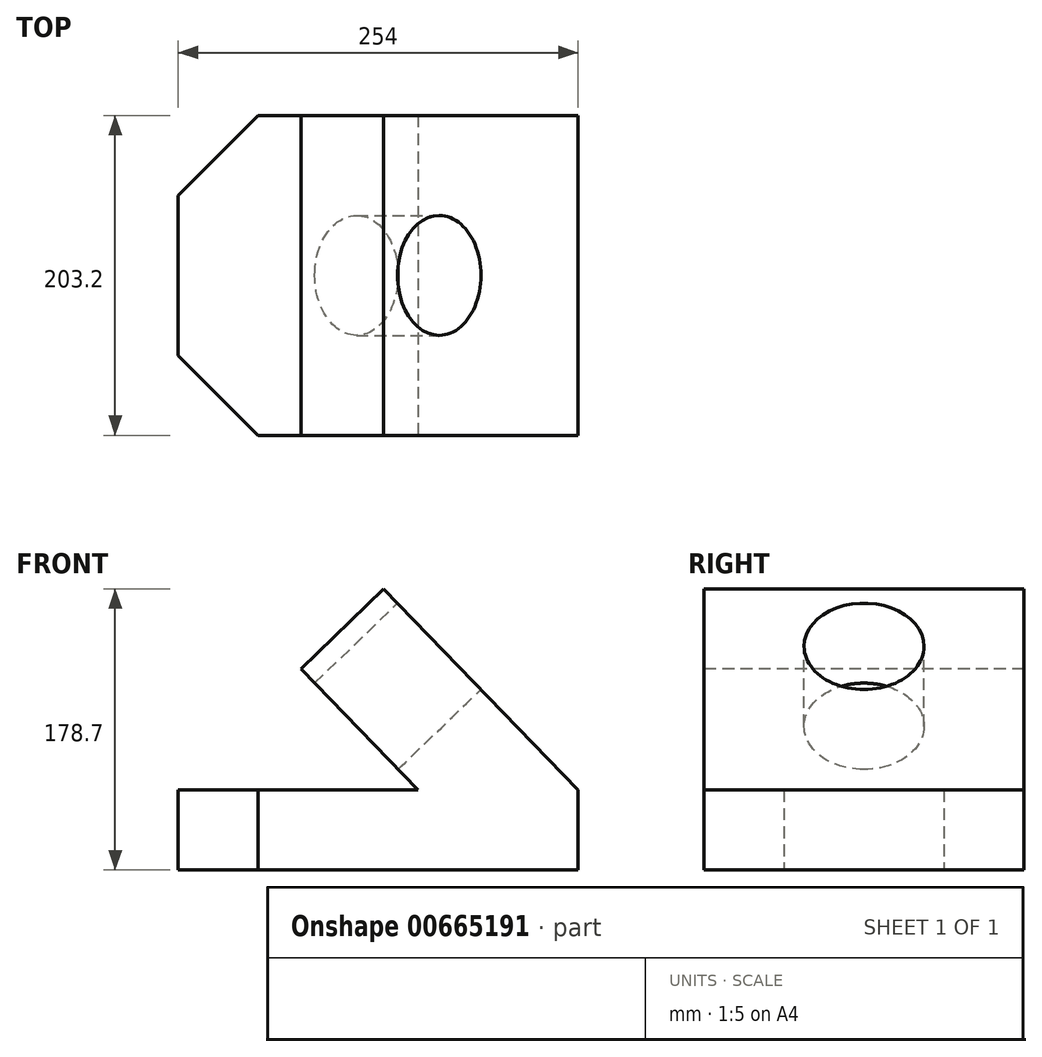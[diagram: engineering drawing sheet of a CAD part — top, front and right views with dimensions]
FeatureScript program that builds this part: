
annotation { "Feature Type Name" : "Feature", "Feature Type Description" : "" }
export const myFeature = defineFeature(function(context is Context, id is Id, definition is map)
    precondition{}
    {
        {
            var Q0;
            Q0=qCreatedBy(makeId("Top.planeOp"),FACE);
            var sketch = newSketch(context, id + "F0", { "sketchPlane" : qUnion([Q0])});
            skLineSegment(sketch, "E0", {"start": v(0, 0) * mm, "end": v(203.2, 0) * mm});
            skLineSegment(sketch, "E1", {"start": v(203.2, 0) * mm, "end": v(203.2, 203.2) * mm});
            skLineSegment(sketch, "E2", {"start": v(203.2, 203.2) * mm, "end": v(0, 203.2) * mm});
            skLineSegment(sketch, "E3", {"start": v(0, 203.2) * mm, "end": v(-50.8, 152.4) * mm});
            skLineSegment(sketch, "E4", {"start": v(-50.8, 152.4) * mm, "end": v(-50.8, 50.8) * mm});
            skLineSegment(sketch, "E5", {"start": v(-50.8, 50.8) * mm, "end": v(0, 0) * mm});
            skSolve(sketch);
        }
        {
            var Q0;
            Q0=makeQuery(id+"F0.imprint","IMPRINT",FACE,{"disambiguationData":[TD([[makeQuery(id+"F0.imprint","IMPRINT",EDGE,{"derivedFrom":sQuery(id+"F0.wireOp",EDGE,"E0")}),1.0]])]});
            extrude(context, id + "F1", {"entities" : qUnion([Q0]), "endBound" : BoundingType.SYMMETRIC, "depth" : 50.8 * mm, "offsetDistance" : 25.4 * mm});
        }
        {
            var Q0;
            Q0=makeQuery(id+"F1.opExtrude","CAP_EDGE",EDGE,{"disambiguationData":[OSD([sQuery(id+"F0.wireOp",EDGE,"E1")])],"isStart":false});
            cPlane(context, id + "F2", {"entities" : qUnion([Q0]), "cplaneType" : CPlaneType.LINE_ANGLE, "offset" : 25.4 * mm, "angle" : 46 * degree, "width" : 152.4 * mm, "height" : 152.4 * mm});
        }
        {
            var Q0;
            Q0=qCreatedBy(id+"F2.planeOp",FACE);
            var sketch = newSketch(context, id + "F3", { "sketchPlane" : qUnion([Q0])});
            skLineSegment(sketch, "E6", {"start": v(203.2, 54.92) * mm, "end": v(0, 54.92) * mm});
            skLineSegment(sketch, "E7", {"start": v(203.2, -122.88) * mm, "end": v(0, -122.88) * mm});
            skLineSegment(sketch, "E8", {"start": v(0, -122.88) * mm, "end": v(0, 54.92) * mm});
            skCircle(sketch, "E9", {"center": v(101.6, 4.12) * mm, "radius": 38.1 * mm});
            skLineSegment(sketch, "E10", {"start": v(203.2, -122.88) * mm, "end": v(203.2, 54.92) * mm});
            skSolve(sketch);
        }
        {
            var Q0;
            Q0=qCreatedBy(makeId("Front.planeOp"),FACE);
            var sketch = newSketch(context, id + "F4", { "sketchPlane" : qUnion([Q0])});
            skPoint(sketch, "E11", {"position": v(101.6, 25.4) * mm});
            skSolve(sketch);
        }
        {
            var Q0;
            Q0=makeQuery(id+"F3.imprint","IMPRINT",FACE,{"disambiguationData":[TD([[makeQuery(id+"F3.imprint","IMPRINT",EDGE,{"derivedFrom":sQuery(id+"F3.wireOp",EDGE,"E6")}),1.0]])]});
            var Q1;
            Q1=sQuery(id+"F4.wireOp",VERTEX,"E11");
            extrude(context, id + "F5", {"entities" : qUnion([Q0]), "operationType" : NewBodyOperationType.ADD, "endBound" : BoundingType.UP_TO_VERTEX, "oppositeDirection" : true, "depth" : 25.4 * mm, "endBoundEntityVertex" : qUnion([Q1]), "offsetDistance" : 25.4 * mm});
        }
    });
